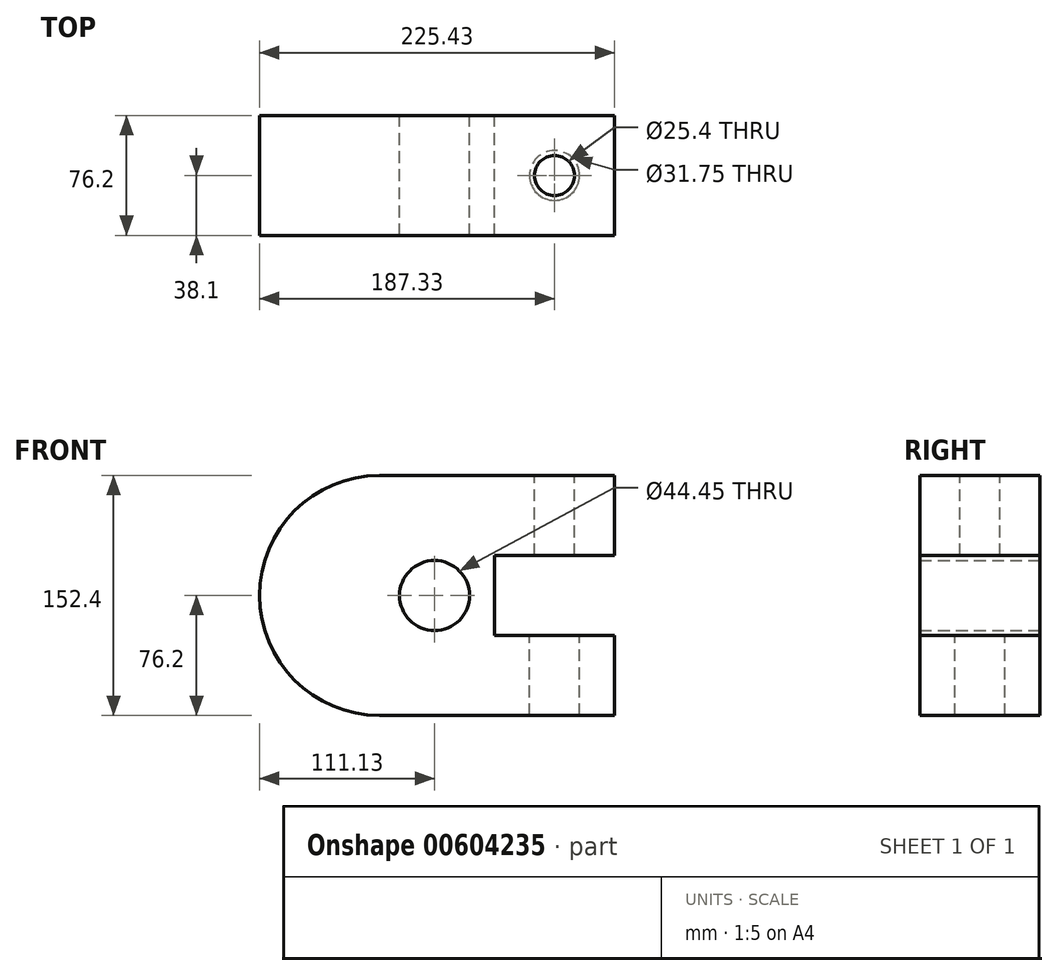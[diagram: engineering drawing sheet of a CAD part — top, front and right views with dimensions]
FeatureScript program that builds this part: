
annotation { "Feature Type Name" : "Feature", "Feature Type Description" : "" }
export const myFeature = defineFeature(function(context is Context, id is Id, definition is map)
    precondition{}
    {
        {
            var Q0;
            Q0=qCreatedBy(makeId("Front.planeOp"),FACE);
            var sketch = newSketch(context, id + "F0", { "sketchPlane" : qUnion([Q0])});
            skLineSegment(sketch, "E0", {"start": v(0, 0) * mm, "end": v(0, 50.8) * mm});
            skLineSegment(sketch, "E1", {"start": v(0, 50.8) * mm, "end": v(-76.2, 50.8) * mm});
            skLineSegment(sketch, "E2", {"start": v(-76.2, 50.8) * mm, "end": v(-76.2, 101.6) * mm});
            skLineSegment(sketch, "E3", {"start": v(-76.2, 101.6) * mm, "end": v(0, 101.6) * mm});
            skLineSegment(sketch, "E4", {"start": v(0, 101.6) * mm, "end": v(0, 152.4) * mm});
            skLineSegment(sketch, "E5", {"start": v(0, 152.4) * mm, "end": v(-149.22, 152.4) * mm});
            skLineSegment(sketch, "E6", {"start": v(0, 0) * mm, "end": v(-149.23, 0) * mm});
            skArc(sketch, "E7", {"start": v(-149.23, 152.4) * mm, "mid": v(-225.43, 76.2) * mm, "end": v(-149.23, 0) * mm});
            skCircle(sketch, "E8", {"center": v(-114.3, 76.2) * mm, "radius": 22.23 * mm});
            skSolve(sketch);
        }
        {
            var Q0;
            Q0=makeQuery(id+"F0.imprint","IMPRINT",FACE,{"disambiguationData":[TD([[makeQuery(id+"F0.imprint","IMPRINT",EDGE,{"derivedFrom":sQuery(id+"F0.wireOp",EDGE,"E0")}),1.0]])]});
            extrude(context, id + "F1", {"entities" : qUnion([Q0]), "depth" : 76.2 * mm, "offsetDistance" : 25.4 * mm});
        }
        {
            var Q0;
            Q0=makeQuery(id+"F1.opExtrude","SWEPT_FACE",FACE,{"disambiguationData":[OSD([sQuery(id+"F0.wireOp",EDGE,"E5")])]});
            var sketch = newSketch(context, id + "F2", { "sketchPlane" : qUnion([Q0])});
            skCircle(sketch, "E9", {"center": v(-38.1, -38.1) * mm, "radius": 12.7 * mm});
            skSolve(sketch);
        }
        {
            var Q0;
            Q0=makeQuery(id+"F1.opExtrude","SWEPT_FACE",FACE,{"disambiguationData":[OSD([sQuery(id+"F0.wireOp",EDGE,"E1")])]});
            var sketch = newSketch(context, id + "F3", { "sketchPlane" : qUnion([Q0])});
            skCircle(sketch, "E10", {"center": v(-38.1, -38.1) * mm, "radius": 15.88 * mm});
            skSolve(sketch);
        }
        {
            var Q0;
            Q0=makeQuery(id+"F2.imprint","IMPRINT",FACE,{"disambiguationData":[TD([[makeQuery(id+"F2.imprint","IMPRINT",EDGE,{"derivedFrom":sQuery(id+"F2.wireOp",EDGE,"E9")}),1.0]])]});
            var Q1;
            Q1=sQuery(id+"F2.wireOp",EDGE,"E9");
            extrude(context, id + "F4", {"entities" : qUnion([Q0]), "operationType" : NewBodyOperationType.REMOVE, "surfaceEntities" : qUnion([Q1]), "oppositeDirection" : true, "depth" : 56.64 * mm, "offsetDistance" : 25.4 * mm});
        }
        {
            var Q0;
            Q0=makeQuery(id+"F3.imprint","IMPRINT",FACE,{"disambiguationData":[TD([[makeQuery(id+"F3.imprint","IMPRINT",EDGE,{"derivedFrom":sQuery(id+"F3.wireOp",EDGE,"E10")}),1.0]])]});
            extrude(context, id + "F5", {"entities" : qUnion([Q0]), "operationType" : NewBodyOperationType.REMOVE, "oppositeDirection" : true, "depth" : 101.6 * mm, "offsetDistance" : 25.4 * mm});
        }
    });
